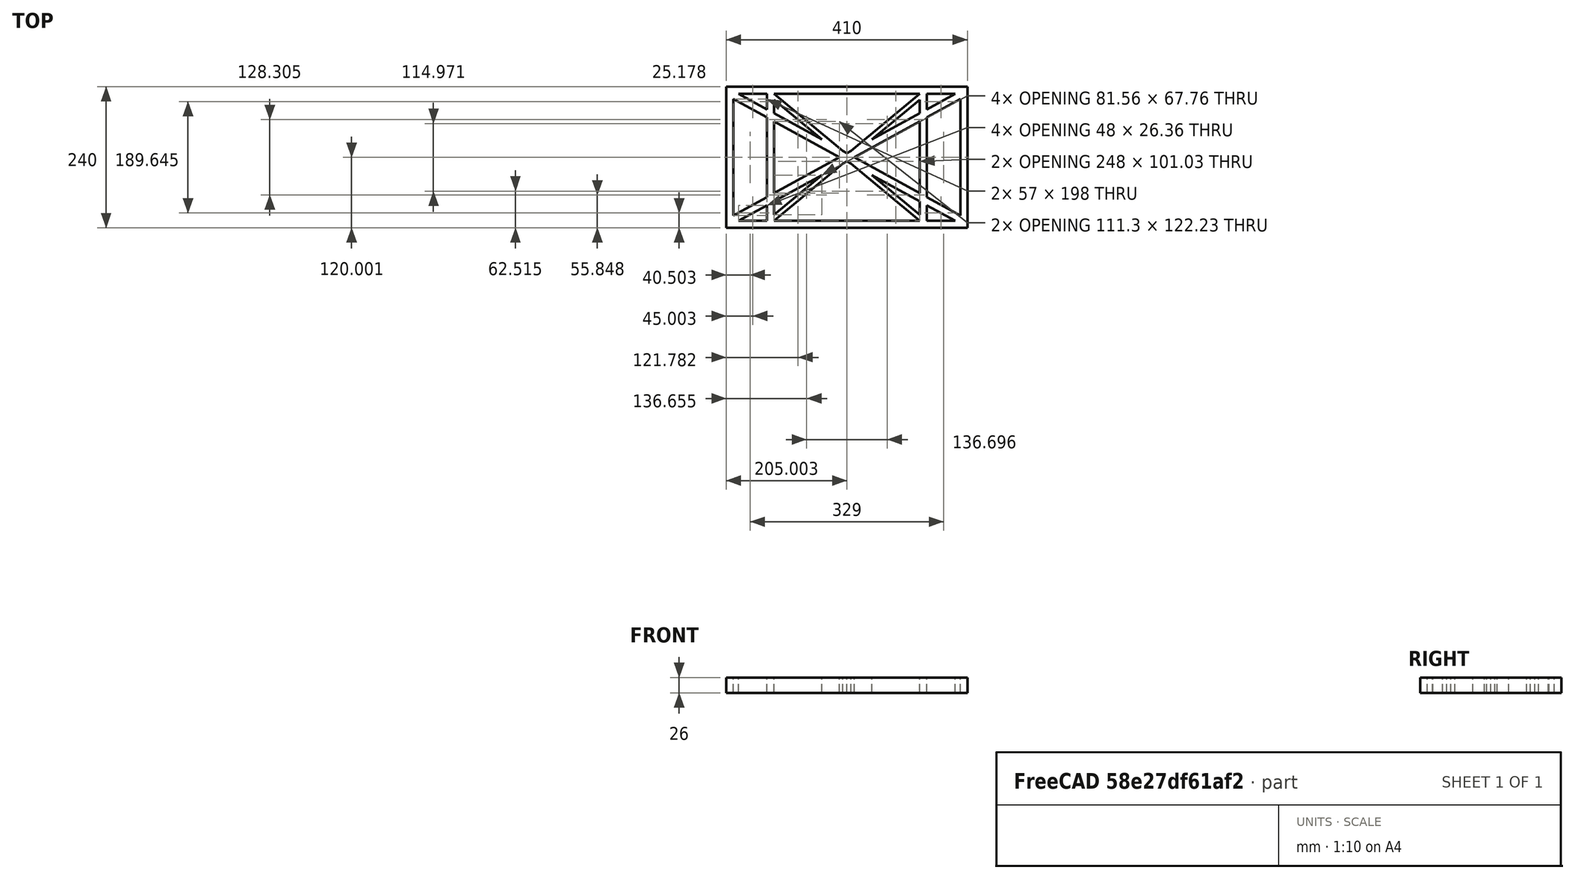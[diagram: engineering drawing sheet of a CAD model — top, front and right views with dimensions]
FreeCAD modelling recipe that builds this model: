
FCSTD DOCUMENT  (FreeCAD 0.19R0.19.2)
Label: laptopStand023
License: All rights reserved
LicenseURL: http://en.wikipedia.org/wiki/All_rights_reserved
objects: Sketcher::SketchObject×3, Part::Extrusion×1
note: 4 computed .brp shape members not serialized (recipe doc carries the construction recipe); baked Part::Feature solids carry a one-line shape summary decoded from their .brp

FEATURE [Sketcher::SketchObject] Sketch
  FullyConstrained = true
  sketch-geometry (52):
    g0: LineSegment StartX=-22.9272 StartY=136.221 StartZ=0 EndX=-22.9272 EndY=-103.779 EndZ=0
    g1: LineSegment StartX=-22.9272 StartY=136.221 StartZ=0 EndX=387.073 EndY=136.221 EndZ=0
    g2: LineSegment StartX=-22.9272 StartY=-103.779 StartZ=0 EndX=387.073 EndY=-103.779 EndZ=0
    g3: LineSegment StartX=387.073 StartY=136.221 StartZ=0 EndX=387.073 EndY=-103.779 EndZ=0
    g4: LineSegment StartX=375.073 StartY=115.221 StartZ=0 EndX=318.073 EndY=83.9235 EndZ=0
    g5: LineSegment StartX=-10.9272 StartY=-82.7794 StartZ=0 EndX=46.0728 EndY=-51.4823 EndZ=0
    g6: LineSegment StartX=-1.92719 StartY=124.221 StartZ=0 EndX=46.0728 EndY=97.8651 EndZ=0
    g7: LineSegment StartX=366.073 StartY=-91.7794 StartZ=0 EndX=318.073 EndY=-65.424 EndZ=0
    g8: LineSegment StartX=-10.9272 StartY=115.221 StartZ=0 EndX=-10.9272 EndY=-82.7794 EndZ=0
    g9: LineSegment StartX=375.073 StartY=-82.7794 StartZ=0 EndX=375.073 EndY=115.221 EndZ=0
    g10: LineSegment StartX=-1.92719 StartY=-91.7794 StartZ=0 EndX=46.0728 EndY=-91.7794 EndZ=0
    g11: LineSegment StartX=318.073 StartY=124.221 StartZ=0 EndX=366.073 EndY=124.221 EndZ=0
    g12: LineSegment StartX=306.073 StartY=-81.8102 StartZ=0 EndX=224.513 EndY=-14.0532 EndZ=0
    g13: LineSegment StartX=58.0728 StartY=114.251 StartZ=0 EndX=139.632 EndY=46.4944 EndZ=0
    g14: LineSegment StartX=306.073 StartY=124.221 StartZ=0 EndX=189.124 EndY=27.0628 EndZ=0
    g15: LineSegment StartX=58.0728 StartY=-91.7794 StartZ=0 EndX=175.022 EndY=5.37834 EndZ=0
    g16: LineSegment StartX=46.0728 StartY=124.221 StartZ=0 EndX=46.0728 EndY=97.8651 EndZ=0
    g17: LineSegment StartX=58.0728 StartY=-81.8102 StartZ=0 EndX=58.0728 EndY=-58.8351 EndZ=0
    g18: LineSegment StartX=318.073 StartY=124.221 StartZ=0 EndX=318.073 EndY=97.8651 EndZ=0
    g19: LineSegment StartX=306.073 StartY=114.251 StartZ=0 EndX=306.073 EndY=91.2763 EndZ=0
    g20: LineSegment StartX=182.073 StartY=23.1914 StartZ=0 EndX=189.124 EndY=27.0628 EndZ=0
    g21: LineSegment StartX=182.073 StartY=9.24976 StartZ=0 EndX=175.022 EndY=5.37834 EndZ=0
    g22: LineSegment StartX=224.513 StartY=46.4944 StartZ=0 EndX=306.073 EndY=114.251 EndZ=0
    g23: LineSegment StartX=175.022 StartY=27.0628 StartZ=0 EndX=58.0728 EndY=124.221 EndZ=0
    g24: LineSegment StartX=169.377 StartY=16.2206 StartZ=0 EndX=58.0728 EndY=77.3346 EndZ=0
    g25: LineSegment StartX=139.632 StartY=-14.0532 StartZ=0 EndX=58.0728 EndY=-81.8102 EndZ=0
    g26: LineSegment StartX=194.768 StartY=16.2206 StartZ=0 EndX=306.073 EndY=-44.8935 EndZ=0
    g27: LineSegment StartX=224.513 StartY=46.4944 StartZ=0 EndX=306.073 EndY=91.2763 EndZ=0
    g28: LineSegment StartX=175.022 StartY=27.0628 StartZ=0 EndX=182.073 EndY=23.1914 EndZ=0
    g29: LineSegment StartX=139.632 StartY=-14.0532 StartZ=0 EndX=58.0728 EndY=-58.8351 EndZ=0
    g30: LineSegment StartX=189.124 StartY=5.37834 StartZ=0 EndX=182.073 EndY=9.24976 EndZ=0
    g31: LineSegment StartX=189.124 StartY=5.37834 StartZ=0 EndX=306.073 EndY=-91.7794 EndZ=0
    g32: LineSegment StartX=306.073 StartY=77.3346 StartZ=0 EndX=306.073 EndY=-44.8935 EndZ=0
    g33: LineSegment StartX=318.073 StartY=83.9235 StartZ=0 EndX=318.073 EndY=-51.4823 EndZ=0
    g34: LineSegment StartX=318.073 StartY=97.8651 StartZ=0 EndX=366.073 EndY=124.221 EndZ=0
    g35: LineSegment StartX=306.073 StartY=77.3346 StartZ=0 EndX=194.768 EndY=16.2206 EndZ=0
    g36: LineSegment StartX=306.073 StartY=-58.8351 StartZ=0 EndX=224.513 EndY=-14.0532 EndZ=0
    g37: LineSegment StartX=306.073 StartY=-58.8351 StartZ=0 EndX=306.073 EndY=-81.8102 EndZ=0
    g38: LineSegment StartX=318.073 StartY=-51.4823 StartZ=0 EndX=375.073 EndY=-82.7794 EndZ=0
    g39: LineSegment StartX=318.073 StartY=-65.424 StartZ=0 EndX=318.073 EndY=-91.7794 EndZ=0
    g40: LineSegment StartX=306.073 StartY=124.221 StartZ=0 EndX=58.0728 EndY=124.221 EndZ=0
    g41: LineSegment StartX=318.073 StartY=-91.7794 StartZ=0 EndX=366.073 EndY=-91.7794 EndZ=0
    g42: LineSegment StartX=58.0728 StartY=-91.7794 StartZ=0 EndX=306.073 EndY=-91.7794 EndZ=0
    g43: LineSegment StartX=58.0728 StartY=-44.8935 StartZ=0 EndX=58.0728 EndY=77.3346 EndZ=0
    g44: LineSegment StartX=46.0728 StartY=-65.424 StartZ=0 EndX=-1.92719 EndY=-91.7794 EndZ=0
    g45: LineSegment StartX=46.0728 StartY=-65.424 StartZ=0 EndX=46.0728 EndY=-91.7794 EndZ=0
    g46: LineSegment StartX=58.0728 StartY=-44.8935 StartZ=0 EndX=169.377 EndY=16.2206 EndZ=0
    g47: LineSegment StartX=58.0728 StartY=91.2763 StartZ=0 EndX=58.0728 EndY=114.251 EndZ=0
    g48: LineSegment StartX=46.0728 StartY=83.9235 StartZ=0 EndX=46.0728 EndY=-51.4823 EndZ=0
    g49: LineSegment StartX=46.0728 StartY=124.221 StartZ=0 EndX=-1.92719 EndY=124.221 EndZ=0
    g50: LineSegment StartX=58.0728 StartY=91.2763 StartZ=0 EndX=139.632 EndY=46.4944 EndZ=0
    g51: LineSegment StartX=46.0728 StartY=83.9235 StartZ=0 EndX=-10.9272 EndY=115.221 EndZ=0
  constraints (102):
    c: Vertical(g0)
    c: Distance(g0) = 240
    c: Horizontal(g1)
    c: Distance(g1) = 410
    c: Coincident(g1,g0)
    c: Coincident(g2,g0)
    c: Horizontal(g2)
    c: Coincident(g3,g1)
    c: Vertical(g3)
    c: Coincident(g2,g3)
    c: Block(g1)
    c: Horizontal(g10)
    c: Horizontal(g11)
    c: PointOnObject(g35,g6)
    c: Coincident(g28,g20)
    c: Coincident(g30,g21)
    c: Tangent(g7,g24)
    c: PointOnObject(g24,g5)
    c: PointOnObject(g26,g4)
    c: Coincident(g20,g14)
    c: Tangent(g20,g27)
    c: Coincident(g50,g13)
    c: Coincident(g28,g23)
    c: Coincident(g22,g27)
    c: Coincident(g21,g15)
    c: Coincident(g29,g25)
    c: Tangent(g21,g29)
    c: Coincident(g36,g12)
    c: Coincident(g31,g30)
    c: Coincident(g22,g19)
    c: Tangent(g19,g32)
    c: Tangent(g18,g33)
    c: Coincident(g27,g19)
    c: Tangent(g27,g34)
    c: Coincident(g4,g33)
    c: Coincident(g35,g32)
    c: Tangent(g4,g35)
    c: Coincident(g37,g12)
    c: Tangent(g7,g36)
    c: Tangent(g32,g37)
    c: Coincident(g26,g32)
    c: Tangent(g26,g38)
    c: Coincident(g33,g38)
    c: Coincident(g39,g7)
    c: Tangent(g33,g39)
    c: Coincident(g25,g17)
    c: Tangent(g17,g43)
    c: Coincident(g29,g17)
    c: Tangent(g29,g44)
    c: Coincident(g45,g44)
    c: Tangent(g16,g45)
    c: Coincident(g5,g48)
    c: Coincident(g46,g43)
    c: Tangent(g5,g46)
    c: Tangent(g43,g47)
    c: Tangent(g16,g48)
    c: Coincident(g13,g47)
    c: PointOnObject(g40,g23)
    c: Tangent(g40,g49)
    c: Coincident(g6,g16)
    c: Coincident(g50,g47)
    c: Tangent(g6,g50)
    c: Coincident(g24,g43)
    c: Coincident(g51,g48)
    c: Tangent(g24,g51)
    c: Block(g23)
    c: Block(g14)
    c: Block(g20)
    c: Block(g40)
    c: Block(g18)
    c: Block(g34)
    c: Block(g4)
    c: Block(g38)
    c: Block(g9)
    c: Block(g36)
    c: Block(g37)
    c: Block(g7)
    c: Block(g39)
    c: Block(g22)
    c: Block(g31)
    c: Block(g42)
    c: Block(g21)
    c: Block(g15)
    c: Block(g29)
    c: Block(g25)
    c: Block(g45)
    c: Block(g44)
    c: Block(g5)
    c: Block(g8)
    c: Block(g51)
    c: Block(g6)
    c: Block(g16)
    c: Block(g13)
    c: Block(g47)
    c: Block(g35)
    c: Block(g32)
    c: Block(g24)
    c: Block(g46)
    c: Block(g49)
    c: Block(g11)
    c: Block(g41)
    c: Block(g10)
FEATURE [Part::Extrusion] Extrude
  Base = -> Sketch
  Dir = (0,0,1)
  DirMode = 2
  FaceMakerClass = Part::FaceMakerBullseye
  LengthFwd = 26
  LengthRev = 0
  Solid = true
  Symmetric = false
FEATURE [Sketcher::SketchObject] Sketch001
  FullyConstrained = false
  MapMode = 4
  Placement = pos=(0,0,0) rot=(0.57735,0.57735,0.57735;2.0944rad)
  Support = -> [Sketch]
  sketch-geometry (25):
    g0: LineSegment StartX=17.2228 StartY=-16.0875 StartZ=0 EndX=117.223 EndY=-16.0875 EndZ=0
    g1: LineSegment StartX=17.2228 StartY=-16.0875 StartZ=0 EndX=17.2228 EndY=-19.0875 EndZ=0
    g2: LineSegment StartX=117.223 StartY=-16.0875 StartZ=0 EndX=117.223 EndY=-19.0875 EndZ=0
    g3: BSplineCurve PolesCount=3 KnotsCount=2 Degree=2 IsPeriodic=0
    g4: LineSegment StartX=94.6577 StartY=-26.1351 StartZ=0 EndX=24.2583 EndY=-213.335 EndZ=0
    g5: LineSegment StartX=-9.4377 StartY=-200.664 StartZ=0 EndX=24.2583 EndY=-213.335 EndZ=0
    g6: LineSegment StartX=-9.4377 StartY=-200.664 StartZ=0 EndX=56.1962 EndY=-26.1351 EndZ=0
    g7: LineSegment StartX=17.2228 StartY=-19.0875 StartZ=0 EndX=38.8094 EndY=-19.0875 EndZ=0
    g8: BSplineCurve PolesCount=4 KnotsCount=2 Degree=3 IsPeriodic=0
    g9: ArcOfCircle CenterX=73.122 CenterY=-32.2909 CenterZ=0 NormalX=0 NormalY=0 NormalZ=1 AngleXU=0 Radius=13 StartAngle=5.92268 EndAngle=9.06428
    g10: ArcOfCircle CenterX=69.5949 CenterY=-41.6481 CenterZ=0 NormalX=0 NormalY=0 NormalZ=1 AngleXU=0 Radius=13.0002 StartAngle=2.78069 EndAngle=5.92131
    g11: LineSegment StartX=60.9577 StartY=-27.7052 StartZ=0 EndX=57.4321 EndY=-37.0574 EndZ=0
    g12: LineSegment StartX=85.2864 StartY=-36.8765 StartZ=0 EndX=81.7532 EndY=-46.2505 EndZ=0
    g13: ArcOfCircle CenterX=123.669 CenterY=-67.4989 CenterZ=0 NormalX=0 NormalY=0 NormalZ=1 AngleXU=0 Radius=13 StartAngle=5.92268 EndAngle=9.06428
    g14: ArcOfCircle CenterX=120.142 CenterY=-76.8561 CenterZ=0 NormalX=0 NormalY=0 NormalZ=1 AngleXU=0 Radius=13 StartAngle=2.78068 EndAngle=5.92131
    g15: LineSegment StartX=111.505 StartY=-62.9133 StartZ=0 EndX=107.979 EndY=-72.2654 EndZ=0
    g16: LineSegment StartX=135.833 StartY=-72.0846 StartZ=0 EndX=132.3 EndY=-81.4585 EndZ=0
    g17: LineSegment StartX=123.669 StartY=-67.4989 StartZ=0 EndX=128.245 EndY=-55.3309 EndZ=0
    g18: ArcOfCircle CenterX=53.8858 CenterY=-83.3902 CenterZ=0 NormalX=0 NormalY=0 NormalZ=1 AngleXU=0 Radius=13 StartAngle=5.92268 EndAngle=9.06428
    g19: ArcOfCircle CenterX=50.3584 CenterY=-92.7474 CenterZ=0 NormalX=0 NormalY=0 NormalZ=1 AngleXU=0 Radius=13 StartAngle=2.78068 EndAngle=5.92131
    g20: LineSegment StartX=41.7214 StartY=-78.8046 StartZ=0 EndX=38.1959 EndY=-88.1567 EndZ=0
    g21: LineSegment StartX=66.0502 StartY=-87.9759 StartZ=0 EndX=62.5164 EndY=-97.3498 EndZ=0
    g22: LineSegment StartX=53.8858 StartY=-83.3902 StartZ=0 EndX=58.4617 EndY=-71.2222 EndZ=0
    g23: LineSegment StartX=53.8858 StartY=-83.3902 StartZ=0 EndX=45.7899 EndY=-104.918 EndZ=0
    g24: LineSegment StartX=45.7899 StartY=-104.918 StartZ=0 EndX=37.6354 EndY=-128.53 EndZ=0
  constraints (53):
    c: Horizontal(g0)
    c: Distance(g0) = 100
    c: Block(g0)
    c: Coincident(g1,g0)
    c: Vertical(g1)
    c: Distance(g1) = 3
    c: Coincident(g2,g0)
    c: Vertical(g2)
    c: Distance(g2) = 3
    c: Block(g3)
    c: Coincident(g3,g2)
    c: Coincident(g4,g3)
    c: Block(g4)
    c: Coincident(g5,g4)
    c: Coincident(g6,g5)
    c: Coincident(g7,g1)
    c: Horizontal(g7)
    c: Block(g8)
    c: Coincident(g8,g7)
    c: Coincident(g8,g6)
    c: Block(g6)
    c: Block(g9)
    c: Block(g10)
    c: Coincident(g11,g9)
    c: Coincident(g11,g10)
    c: Coincident(g12,g9)
    c: Coincident(g12,g10)
    c: Block(g12)
    c: Block(g11)
    c: Block(g13)
    c: Block(g14)
    c: Coincident(g15,g13)
    c: Coincident(g15,g14)
    c: Coincident(g16,g13)
    c: Coincident(g16,g14)
    c: Block(g16)
    c: Block(g15)
    c: Coincident(g17,g13)
    c: PointOnObject(g17,g13)
    c: Block(g18)
    c: Block(g19)
    c: Coincident(g20,g18)
    c: Coincident(g20,g19)
    c: Coincident(g21,g18)
    c: Coincident(g21,g19)
    c: Block(g21)
    c: Block(g20)
    c: Coincident(g22,g18)
    c: PointOnObject(g22,g18)
    c: Coincident(g23,g18)
    c: Parallel(g4,g23)
    c: PointOnObject(g23,g19)
    c: Coincident(g24,g23)
FEATURE [Sketcher::SketchObject] Sketch002
  FullyConstrained = true
  Placement = pos=(0,0,0) rot=(-1,0,0;4.71239rad)
